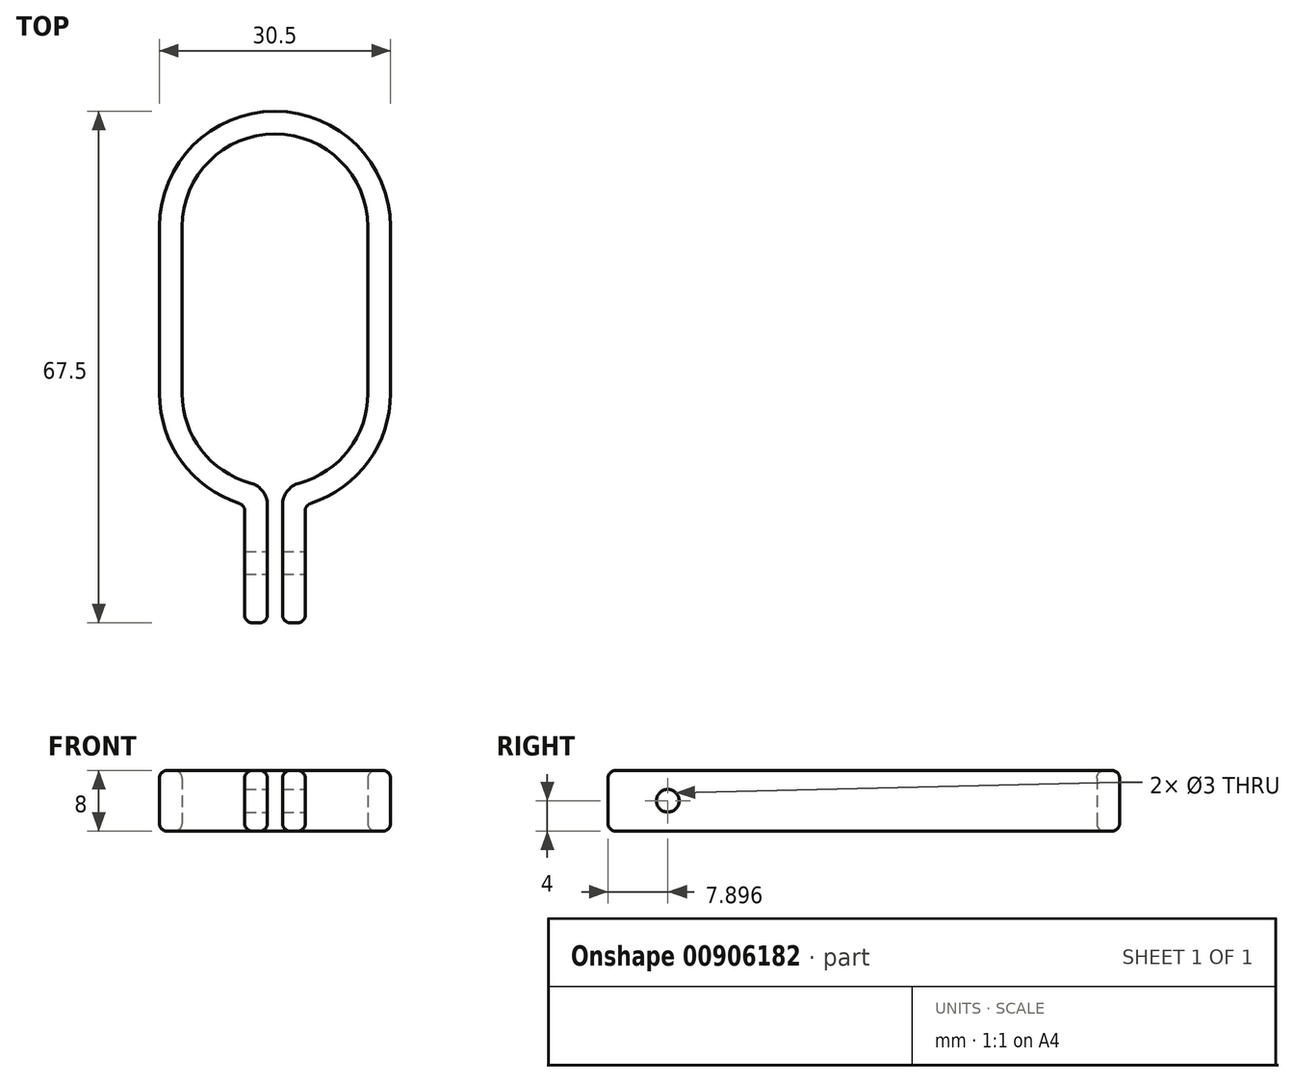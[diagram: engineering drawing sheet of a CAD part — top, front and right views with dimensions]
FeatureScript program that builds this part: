
annotation { "Feature Type Name" : "Feature", "Feature Type Description" : "" }
export const myFeature = defineFeature(function(context is Context, id is Id, definition is map)
    precondition{}
    {
        {
            var Q0;
            Q0=qCreatedBy(makeId("Top.planeOp"),FACE);
            var sketch = newSketch(context, id + "F0", { "sketchPlane" : qUnion([Q0])});
            skArc(sketch, "E0", {"start": v(-11.06, 14.07) * mm, "mid": v(-23.31, 26.32) * mm, "end": v(-35.56, 14.07) * mm});
            skArc(sketch, "E1", {"start": v(-35.56, -7.93) * mm, "mid": v(-33.04, -15.37) * mm, "end": v(-26.53, -19.75) * mm});
            skLineSegment(sketch, "E2", {"start": v(-35.56, -7.93) * mm, "end": v(-35.56, 14.07) * mm});
            skLineSegment(sketch, "E3", {"start": v(-11.06, 14.07) * mm, "end": v(-11.06, -7.93) * mm});
            skArc(sketch, "E4.0", {"start": v(-8.06, 14.07) * mm, "mid": v(-23.31, 29.32) * mm, "end": v(-38.56, 14.07) * mm});
            skLineSegment(sketch, "E4.1", {"start": v(-8.06, 14.07) * mm, "end": v(-8.06, -7.93) * mm});
            skArc(sketch, "E4.2", {"start": v(-38.56, -7.93) * mm, "mid": v(-35.64, -16.9) * mm, "end": v(-28, -22.44) * mm});
            skLineSegment(sketch, "E4.3", {"start": v(-38.56, -7.93) * mm, "end": v(-38.56, 14.07) * mm});
            skLineSegment(sketch, "E5.0", {"start": v(-27.31, -23.18) * mm, "end": v(-27.31, -23.4) * mm});
            skLineSegment(sketch, "E6.0", {"start": v(-19.31, -23.18) * mm, "end": v(-19.31, -23.4) * mm});
            skLineSegment(sketch, "E7", {"start": v(-27.31, -23.18) * mm, "end": v(-27.31, -37.18) * mm});
            skLineSegment(sketch, "E8", {"start": v(-19.31, -23.18) * mm, "end": v(-19.31, -37.18) * mm});
            skLineSegment(sketch, "E9.0", {"start": v(-24.31, -23.18) * mm, "end": v(-24.31, -37.18) * mm});
            skLineSegment(sketch, "E9.1", {"start": v(-24.31, -22.64) * mm, "end": v(-24.31, -23.18) * mm});
            skLineSegment(sketch, "E10.0", {"start": v(-22.31, -23.18) * mm, "end": v(-22.31, -37.18) * mm});
            skLineSegment(sketch, "E10.1", {"start": v(-22.31, -22.64) * mm, "end": v(-22.31, -23.18) * mm});
            skLineSegment(sketch, "E11", {"start": v(-26.31, -38.18) * mm, "end": v(-25.31, -38.18) * mm});
            skLineSegment(sketch, "E12", {"start": v(-21.31, -38.18) * mm, "end": v(-20.31, -38.18) * mm});
            skPoint(sketch, "E13.end.orphan", {"position": v(-23.31, -23.18) * mm});
            skArc(sketch, "E14.trimOffspring", {"start": v(-20.1, -19.75) * mm, "mid": v(-13.58, -15.37) * mm, "end": v(-11.06, -7.93) * mm});
            skArc(sketch, "E15.trimOffspring", {"start": v(-18.62, -22.44) * mm, "mid": v(-10.98, -16.9) * mm, "end": v(-8.06, -7.93) * mm});
            skPoint(sketch, "E16.visualSharp", {"position": v(-27.31, -22.64) * mm});
            skArc(sketch, "E16.filletArc", {"start": v(-27.31, -23.4) * mm, "mid": v(-27.5, -22.8) * mm, "end": v(-28, -22.44) * mm});
            skPoint(sketch, "E17.visualSharp", {"position": v(-19.31, -22.64) * mm});
            skArc(sketch, "E17.filletArc", {"start": v(-18.62, -22.44) * mm, "mid": v(-19.12, -22.8) * mm, "end": v(-19.31, -23.4) * mm});
            skPoint(sketch, "E18.visualSharp", {"position": v(-27.31, -38.18) * mm});
            skArc(sketch, "E18.filletArc", {"start": v(-27.31, -37.18) * mm, "mid": v(-27.02, -37.89) * mm, "end": v(-26.31, -38.18) * mm});
            skPoint(sketch, "E19.visualSharp", {"position": v(-24.31, -38.18) * mm});
            skArc(sketch, "E19.filletArc", {"start": v(-25.31, -38.18) * mm, "mid": v(-24.6, -37.89) * mm, "end": v(-24.31, -37.18) * mm});
            skPoint(sketch, "E20.visualSharp", {"position": v(-19.31, -38.18) * mm});
            skArc(sketch, "E20.filletArc", {"start": v(-20.31, -38.18) * mm, "mid": v(-19.6, -37.89) * mm, "end": v(-19.31, -37.18) * mm});
            skPoint(sketch, "E21.visualSharp", {"position": v(-22.31, -38.18) * mm});
            skArc(sketch, "E21.filletArc", {"start": v(-22.31, -37.18) * mm, "mid": v(-22.02, -37.89) * mm, "end": v(-21.31, -38.18) * mm});
            skPoint(sketch, "E22.visualSharp", {"position": v(-24.31, -20.14) * mm});
            skArc(sketch, "E22.filletArc", {"start": v(-24.31, -22.64) * mm, "mid": v(-24.93, -20.82) * mm, "end": v(-26.53, -19.75) * mm});
            skPoint(sketch, "E23.visualSharp", {"position": v(-22.31, -20.14) * mm});
            skArc(sketch, "E23.filletArc", {"start": v(-20.1, -19.75) * mm, "mid": v(-21.7, -20.82) * mm, "end": v(-22.31, -22.64) * mm});
            skSolve(sketch);
        }
        {
            var Q0;
            Q0=makeQuery(id+"F0.imprint","IMPRINT",FACE,{"disambiguationData":[TD([[makeQuery(id+"F0.imprint","IMPRINT",EDGE,{"derivedFrom":sQuery(id+"F0.wireOp",EDGE,"E0")}),-1.0]])]});
            extrude(context, id + "F1", {"entities" : qUnion([Q0]), "depth" : 8 * mm, "offsetDistance" : 25 * mm});
        }
        {
            var Q0;
            Q0=makeQuery(id+"F1.opExtrude","SWEPT_FACE",FACE,{"disambiguationData":[OSD([sQuery(id+"F0.wireOp",EDGE,"E8")])]});
            var sketch = newSketch(context, id + "F2", { "sketchPlane" : qUnion([Q0])});
            skLineSegment(sketch, "E24", {"start": v(-30.28, 4) * mm, "end": v(-23.4, 0) * mm});
            skLineSegment(sketch, "E25", {"start": v(-23.4, 8) * mm, "end": v(-37.18, 0) * mm});
            skSolve(sketch);
        }
        {
            var Q0;
            Q0=sQuery(id+"F2.wireOp",VERTEX,"E24.start");
            var Q1;
            Q1=makeQuery(id+"F1.opExtrude","SWEPT_BODY",BODY,{"disambiguationData":[OSD([sQuery(id+"F0.wireOp",EDGE,"E0"),sQuery(id+"F0.wireOp",EDGE,"E1"),sQuery(id+"F0.wireOp",EDGE,"E2"),sQuery(id+"F0.wireOp",EDGE,"E3"),sQuery(id+"F0.wireOp",EDGE,"E4.0"),sQuery(id+"F0.wireOp",EDGE,"E4.1"),sQuery(id+"F0.wireOp",EDGE,"E4.2"),sQuery(id+"F0.wireOp",EDGE,"E4.3"),sQuery(id+"F0.wireOp",EDGE,"E7"),sQuery(id+"F0.wireOp",EDGE,"E8"),sQuery(id+"F0.wireOp",EDGE,"E9.0"),sQuery(id+"F0.wireOp",EDGE,"E9.1"),sQuery(id+"F0.wireOp",EDGE,"E10.0"),sQuery(id+"F0.wireOp",EDGE,"E10.1"),sQuery(id+"F0.wireOp",EDGE,"E11"),sQuery(id+"F0.wireOp",EDGE,"E12"),sQuery(id+"F0.wireOp",EDGE,"E14.trimOffspring"),sQuery(id+"F0.wireOp",EDGE,"E15.trimOffspring"),sQuery(id+"F0.wireOp",EDGE,"E16.filletArc"),sQuery(id+"F0.wireOp",EDGE,"E17.filletArc"),sQuery(id+"F0.wireOp",EDGE,"E18.filletArc"),sQuery(id+"F0.wireOp",EDGE,"E19.filletArc"),sQuery(id+"F0.wireOp",EDGE,"E20.filletArc"),sQuery(id+"F0.wireOp",EDGE,"E21.filletArc"),sQuery(id+"F0.wireOp",EDGE,"E22.filletArc"),sQuery(id+"F0.wireOp",EDGE,"E23.filletArc")])]});
            hole(context, id + "F3", {"style" : HoleStyle.SIMPLE, "endStyle" : HoleEndStyle.BLIND, "holeDiameter" : 3 * mm, "majorDiameter" : 3 * mm, "holeDepth" : 19.4 * mm, "isTappedThrough" : true, "tappedDepth" : 17.9 * mm, "tapClearance" : 3, "startFromSketch" : true, "locations" : qUnion([Q0]), "scope" : qUnion([Q1])});
        }
        {
            var Q0;
            Q0=makeQuery(id+"F1.opExtrude","CAP_EDGE",EDGE,{"disambiguationData":[OSD([sQuery(id+"F0.wireOp",EDGE,"E4.3")])],"isStart":false});
            var Q1;
            Q1=makeQuery(id+"F1.opExtrude","CAP_EDGE",EDGE,{"disambiguationData":[OSD([sQuery(id+"F0.wireOp",EDGE,"E15.trimOffspring")])],"isStart":true});
            fillet(context, id + "F4", {"entities" : qUnion([Q0, Q1]), "radius" : 1 * mm, "tangentPropagation" : true, "allowEdgeOverflow" : false});
        }
    });
